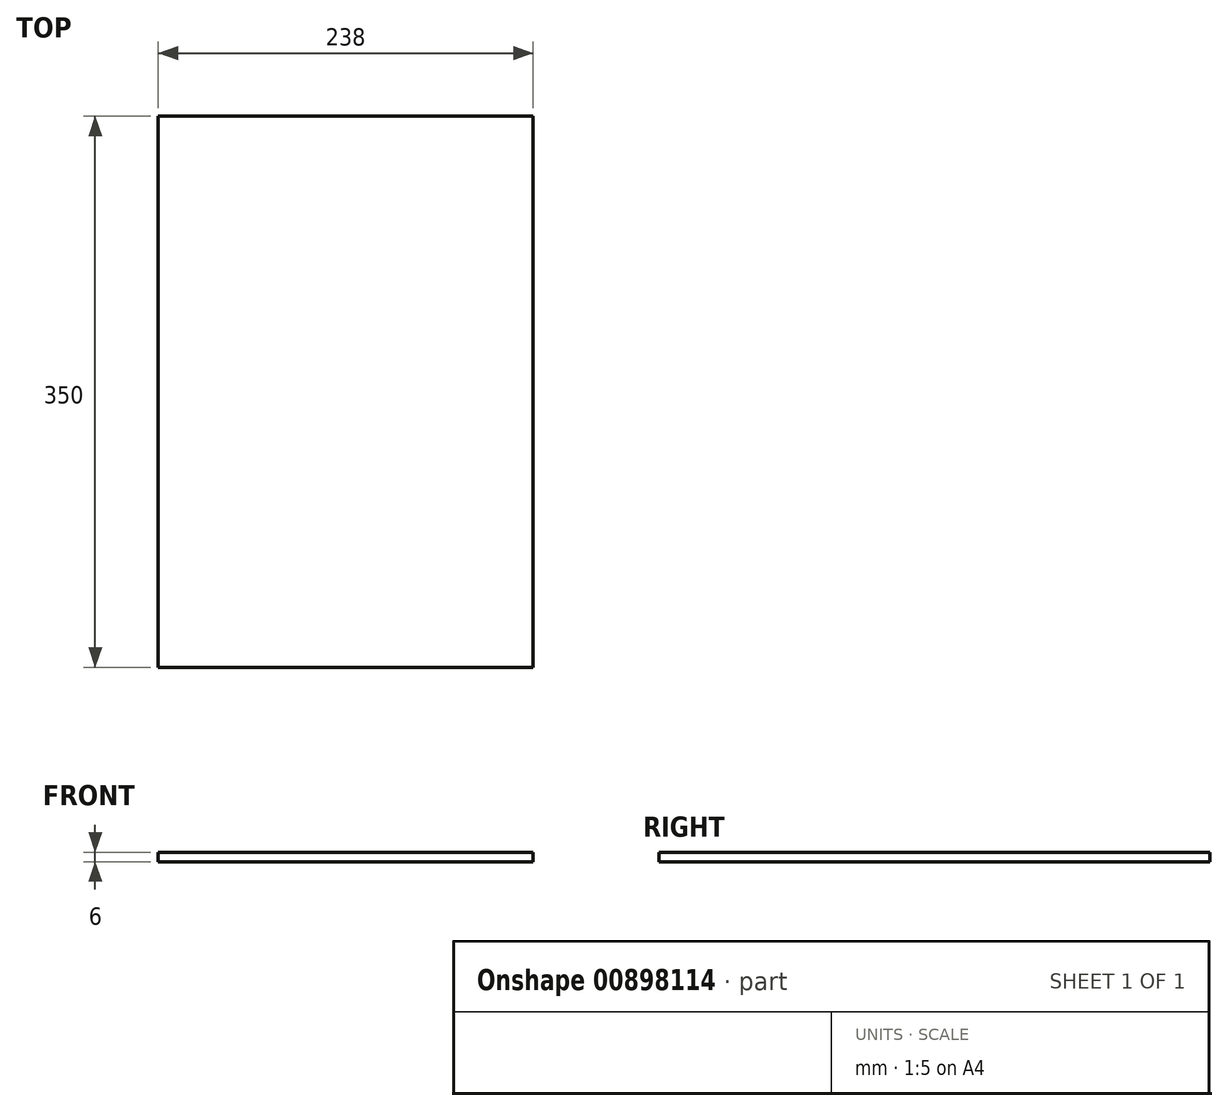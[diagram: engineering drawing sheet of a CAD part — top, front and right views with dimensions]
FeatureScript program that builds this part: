
annotation { "Feature Type Name" : "Feature", "Feature Type Description" : "" }
export const myFeature = defineFeature(function(context is Context, id is Id, definition is map)
    precondition{}
    {
        {
            var Q0;
            Q0=qCreatedBy(makeId("Front.planeOp"),FACE);
            var sketch = newSketch(context, id + "F0", { "sketchPlane" : qUnion([Q0])});
            skLineSegment(sketch, "E0.bottom", {"start": v(0, 0) * mm, "end": v(238, 0) * mm});
            skLineSegment(sketch, "E0.top", {"start": v(0, 6) * mm, "end": v(238, 6) * mm});
            skLineSegment(sketch, "E0.left", {"start": v(0, 0) * mm, "end": v(0, 6) * mm});
            skLineSegment(sketch, "E0.right", {"start": v(238, 0) * mm, "end": v(238, 6) * mm});
            skSolve(sketch);
        }
        {
            var Q0;
            Q0 = qSketchRegion(id + "F0", true);
            extrude(context, id + "F1", {"entities" : qUnion([Q0]), "oppositeDirection" : true, "depth" : 350 * mm, "offsetDistance" : 25 * mm});
        }
    });
